# Revit family: TYCO-FPP-Zettler-QMO850 Quad monitored output module
name_source: partatom
category: Electrical Fixtures
revit_build: Autodesk Revit 2014 (Build: 20130308_1515(x64)
units: mm (PartAtom-declared; Revit-internal decimal feet)

## types (1)
- TYCO-FPP-Zettler-QMO850 Quad monitored output module
    Alarm current = 6.7 mA
    Approvals = EN54-17 and EN54-18
    Battery Requirements = Standby current
2.1 mA
    Description = Quad Monitored Output Module (QMO850)
    Device Mode for each = Sounders
    Keynote = The Quad Monitored Output Module connects directly
to the MZX Digital loop and requires a 24Vdc or 48Vdc
power supply.
    Length = 103 mm
    Manufacturer = Tyco
    Max. switching power = 60 W, 125 VA
    Model = Zettler -555.800.070
    Nominal switching capacity = 2 A 30 VDC
    Operating Humidity = Up to 95 %
    Operating Temperature = -25 to +70 oC
    PCB = PCB
    RS = RS
    RSS = res
    ST = ST12
    Storage Temparature = 40 to +80 oC
    Type Comments = Input-/Output device with Short-
Circuit Isolator for use in fire
detection and alarm systems in
buildings
    URL = https://tycosafetyproducts-anz.com
    Width = 134 mm
    Wire Size = Min. 0.5 mm2, max. 2.5 mm2
    single output point = Door Control

## geometry (parser evidence)
native form markers: Sweep x1
no freeform markers — native parametric forms only
